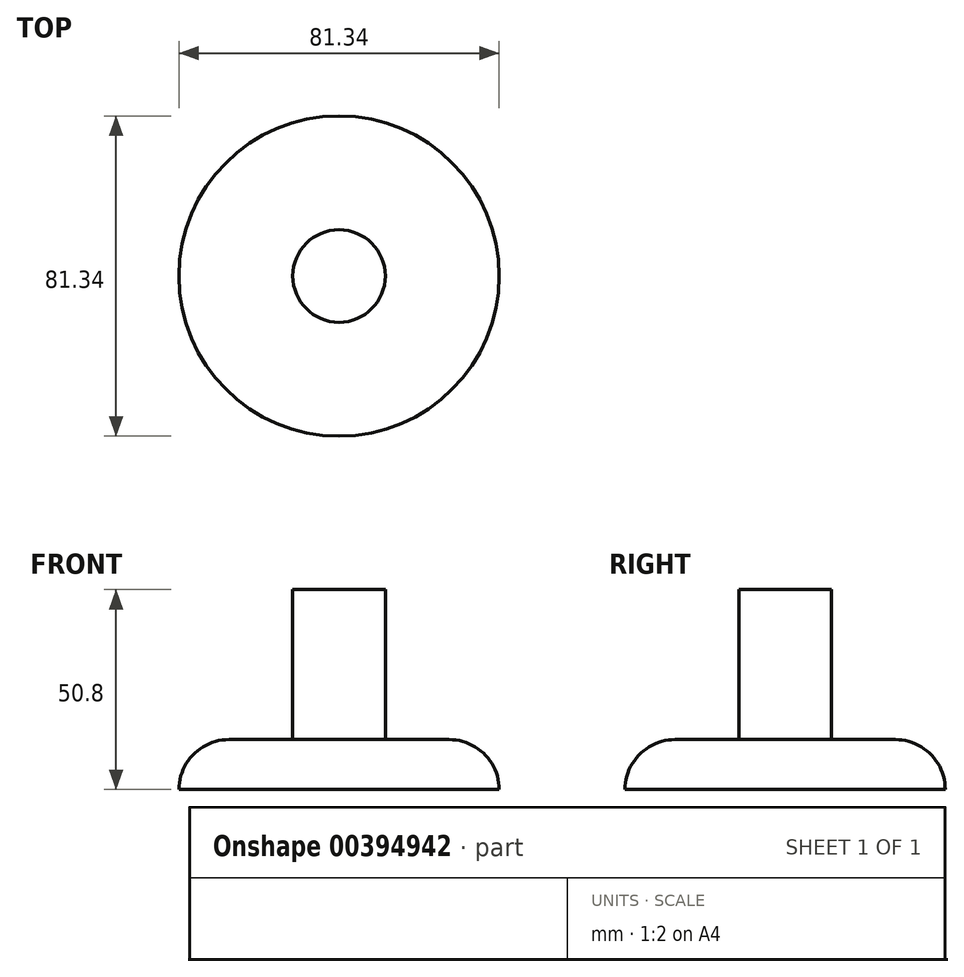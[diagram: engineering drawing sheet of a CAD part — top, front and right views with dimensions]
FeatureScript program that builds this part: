
annotation { "Feature Type Name" : "Feature", "Feature Type Description" : "" }
export const myFeature = defineFeature(function(context is Context, id is Id, definition is map)
    precondition{}
    {
        {
            var Q0;
            Q0=qCreatedBy(makeId("Top.planeOp"),FACE);
            var sketch = newSketch(context, id + "F0", { "sketchPlane" : qUnion([Q0])});
            skCircle(sketch, "E0", {"center": v(0, 0) * mm, "radius": 40.67 * mm});
            skCircle(sketch, "E1", {"center": v(0, 0) * mm, "radius": 11.76 * mm});
            skSolve(sketch);
        }
        {
            var Q0;
            Q0 = qSketchRegion(id + "F0", true);
            extrude(context, id + "F1", {"entities" : qUnion([Q0]), "depth" : 12.7 * mm});
        }
        {
            var Q0;
            Q0=makeQuery(id+"F1.opExtrude","CAP_EDGE",EDGE,{"disambiguationData":[OSD([sQuery(id+"F0.wireOp",EDGE,"E0")])],"isStart":false});
            fillet(context, id + "F2", {"entities" : qUnion([Q0]), "radius" : 12.7 * mm, "tangentPropagation" : true, "allowEdgeOverflow" : false});
        }
        {
            var Q0;
            Q0=makeQuery(id+"F0.imprint","IMPRINT",FACE,{"disambiguationData":[TD([[makeQuery(id+"F0.imprint","IMPRINT",EDGE,{"derivedFrom":sQuery(id+"F0.wireOp",EDGE,"E1")}),1.0]])]});
            extrude(context, id + "F3", {"entities" : qUnion([Q0]), "operationType" : NewBodyOperationType.ADD, "depth" : 50.8 * mm});
        }
        {
            var Q0;
            Q0=qCreatedBy(makeId("Front.planeOp"),FACE);
            var sketch = newSketch(context, id + "F4", { "sketchPlane" : qUnion([Q0])});
            skArc(sketch, "E2", {"start": v(-69.2, 116.79) * mm, "mid": v(-46.6, 70.33) * mm, "end": v(0, 48) * mm});
            skSolve(sketch);
        }
        {
            var Q0;
            Q0 = qSketchRegion(id + "F4", true);
            var Q1;
            Q1=sQuery(id+"F4.wireOp",EDGE,"E2");
            var Q2;
            Q2=makeQuery(id+"F3.opExtrude","CAP_EDGE",EDGE,{"disambiguationData":[OSD([sQuery(id+"F0.wireOp",EDGE,"E1")])],"isStart":false});
            revolve(context, id + "F5", {"bodyType" : ToolBodyType.SURFACE, "entities" : qUnion([Q0]), "surfaceEntities" : qUnion([Q1]), "axis" : qUnion([Q2]), "revolveType" : RevolveType.FULL});
        }
    });
